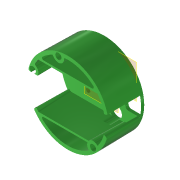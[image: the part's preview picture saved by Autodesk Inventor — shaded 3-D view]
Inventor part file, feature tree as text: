
AUTODESK INVENTOR PART (.ipt)
format: ipt  version: 2022 (Build 260153000, 153)  size: 604,160 bytes
history: native  units: in
note: dims shown in document units (in); Inventor stores cm internally (conversion verified against a paired STEP export)
features: extrude x13, sketch x13, plane x5, reference x3, other x3, projected_geometry x2, fillet x1
ambient origin geometry x8: Origin, YZ Plane, XZ Plane, XY Plane, X Axis, Y Axis, Z Axis, Center Point
bodies: Solid1 (feature_tree)
feature tree (40):
  plane  "Arbeitsebene6"
  extrude  "Extrusion1"  Depth=0.0787in
  extrude  "Extrusion2"  Depth=1.0in
  plane  "Arbeitsebene3"
  extrude  "Extrusion6"  Depth=0.1102in
  plane  "Arbeitsebene2"
  extrude  "Extrusion7"  Depth=0.0787in
  extrude  "Extrusion10"  Depth=0.0394in TaperAngle=0.0deg
  plane  "Arbeitsebene7"
  sketch  "Skizze16"  dims[d81=0.0591in d82=0.3937in d83=0.0069in]
  plane  "Arbeitsebene5"
  extrude  "Extrusion14"  Depth=0.3937in
  extrude  "Extrusion15"  Depth=0.0787in
  extrude  "Extrusion17"  TaperAngle=0.0deg  [1 undecoded]
  extrude  "Extrusion18"  Depth=0.1575in
  extrude  "Extrusion19"  Depth=0.1575in
  extrude  "Extrusion20"  Depth=0.8465in TaperAngle=0.0deg
  fillet  "Rundung2"  Radius=0.1614in
  extrude  "Extrusion21"  Depth=0.1614in
  extrude  "Extrusion22"  Depth=0.0394in
  sketch  "Sketch1"  dims[d0=0.0787in d1=-0.0069in d2=0.315in]
  sketch  "Sketch2"  dims[d3=0.3189in d4=1.0in d5=-0.0137in]
  sketch  "Sketch8"  dims[d33=0.1102in d34=0.1102in]
  sketch  "Sketch9"  dims[d35=0.0in d36=0.0in d37=0.0787in]
  sketch  "Skizze12"  dims[d38=0.0004in d39=-0.0069in d51=0.0394in d52=0.0in]
  sketch  "Skizze17"  dims[d89=0.3937in d90=-0.0069in d91=0.0787in]
  reference  "Referenz44"
  reference  "Referenz45"
  projected_geometry  "Projizierte Kontur4"
  sketch  "Skizze19"  dims[d92=0.0787in d93=0.0in]
  sketch  "Skizze20"  dims[d94=0.0in d104=0.1575in]
  sketch  "Skizze21"  dims[d105=0.1575in d106=0.1575in]
  sketch  "Skizze22"  dims[d107=0.0001in d108=-0.0069in d109=0.8465in d110=0.0in d111=0.1614in]
  reference  "Referenz46"
  sketch  "Skizze23"  dims[d112=0.1614in d113=0.1614in]
  sketch  "Skizze24"  dims[d114=0.1969in d115=-0.0069in d116=0.315in d117=0.315in d118=0.0069in d119=0.0394in d120=0.0394in d122=0.9055in d123=0.4528in d124=1.8701in d125=0.2756in d126=0.4724in d127=0.5906in d128=0.0394in d129=0.0in d130=0.315in d131=0.315in d132=0.1102in d133=0.1102in d134=0.0in d135=0.0in d78=0.0197in d79=0.0344in d80=0.0197in d95=0.0197in d96=0.0344in d97=0.0197in d98=0.0344in]
  projected_geometry  "Projizierte Kontur5"
  other  "Matchboxscope_VCM_v1.iam"
  other  "Matchboxscope_bottom_v0:2"
  other  "Matchboxscope_middle2_m12VCMLens_v2:2"
note: 1 required parameter value undecoded (feature->parameter linkage not recoverable at this tier; creation-order binding heuristic only, values carry confidence <= 0.55)
